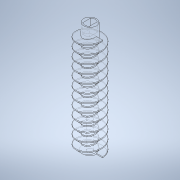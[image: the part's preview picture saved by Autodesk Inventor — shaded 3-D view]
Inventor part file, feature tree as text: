
AUTODESK INVENTOR PART (.ipt)
format: ipt  version: 2022 (Build 260153000, 153)  size: 613,376 bytes
history: native  units: mm
features: sketch x7, extrude x5, other x4, projected_geometry x3, reference x2, mirror x1, sweep x1, chamfer x1
ambient origin geometry x8: Origin, YZ Plane, XZ Plane, XY Plane, X Axis, Y Axis, Z Axis, Center Point
bodies: Solid1 (feature_tree)
feature tree (24):
  extrude  "Extrusion1"  Depth=10.0mm
  sketch  "3D Sketch1"
  extrude  "Extrusion2"  Depth=50.5mm
  mirror  "Mirror1"
  sweep  "Sweep1"
  chamfer  "Chamfer1"  Distance=3.5mm Angle=45.0deg
  extrude  "Extrusion3"  Depth=5.0mm
  extrude  "Extrusion4"  Depth=0.3mm
  extrude  "Extrusion6"  Depth=5.0mm TaperAngle=0.0deg
  sketch  "Sketch1"  dims[d2=0.0mm d3=10.0mm]
  other  "Helical Curve1"
  sketch  "Sketch2"  dims[d6=0.0mm d7=50.5mm]
  projected_geometry  "Projected Loop1"
  sketch  "Sketch3"  dims[d9=0.0mm d10=0.0mm d11=0.0mm d12=3.5mm d13=2.0mm d14=45.0deg]
  projected_geometry  "Projected Loop2"
  sketch  "Sketch4"  dims[d15=5.0mm d16=0.0mm d17=3.3mm]
  projected_geometry  "Projected Loop3"
  sketch  "Sketch5"  dims[d18=15.0mm d19=0.0mm d24=0.3mm]
  sketch  "Sketch7"  dims[d25=0.3mm d26=5.0mm d27=0.0mm]
  reference  "Reference1"
  reference  "Reference2"
  other  "<userpath>\OneDrive - Imperial College London\ROBOICP MK2\solids feeder assembly.iam"
  other  "solids feeder assembly.iam"
  other  "smol stepper:1"
